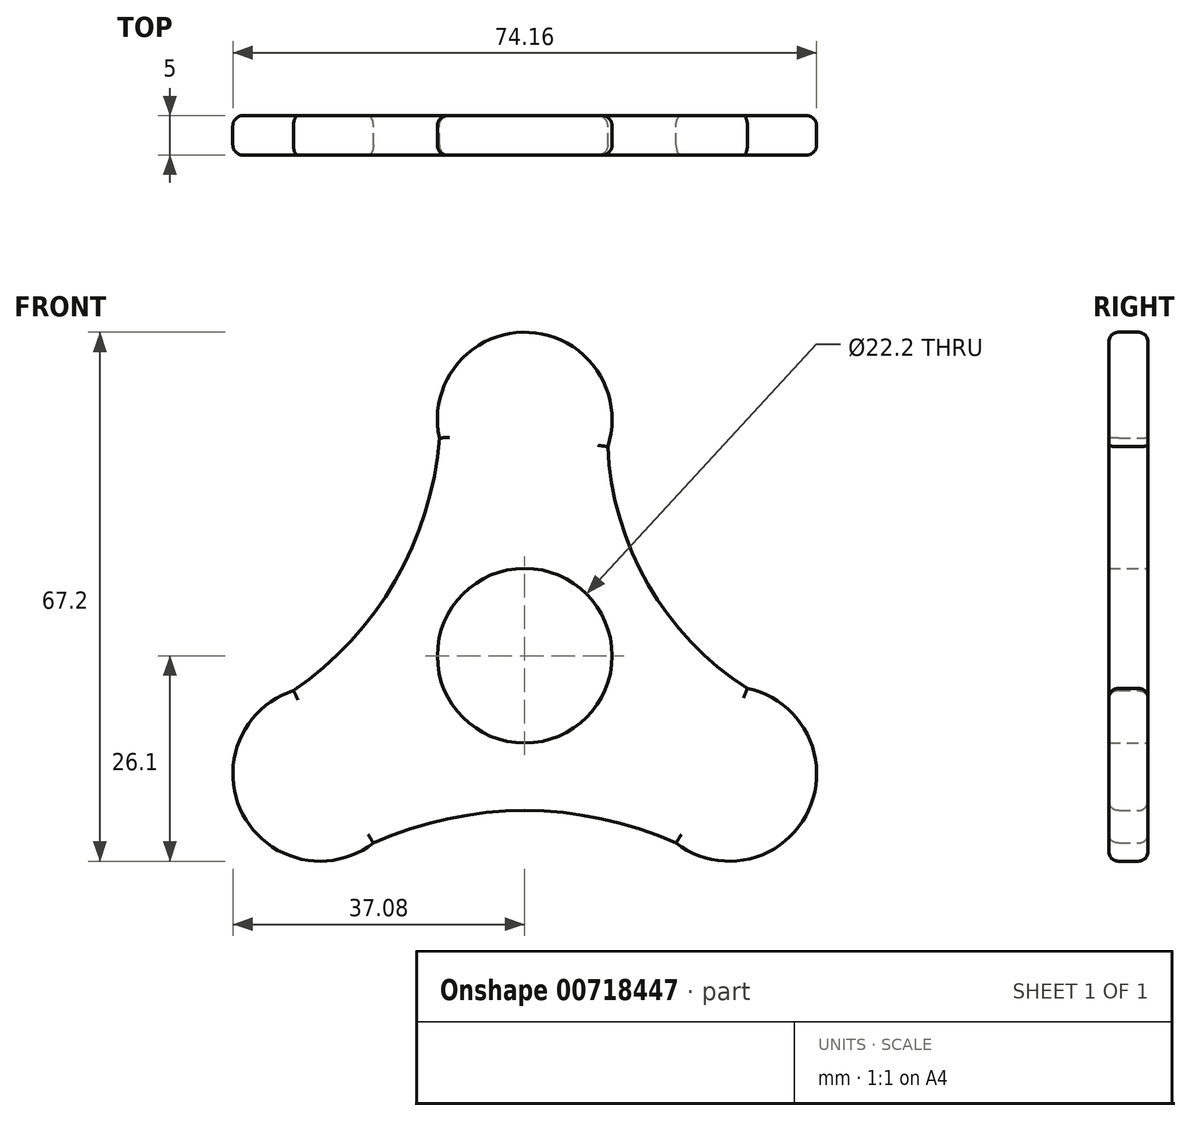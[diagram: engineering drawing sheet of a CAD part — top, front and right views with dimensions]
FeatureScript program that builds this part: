
annotation { "Feature Type Name" : "Feature", "Feature Type Description" : "" }
export const myFeature = defineFeature(function(context is Context, id is Id, definition is map)
    precondition{}
    {
        {
            var Q0;
            Q0=qCreatedBy(makeId("Front.planeOp"),FACE);
            var sketch = newSketch(context, id + "F0", { "sketchPlane" : qUnion([Q0])});
            skCircle(sketch, "E0", {"center": v(0, 0) * mm, "radius": 11.1 * mm});
            skArc(sketch, "E1", {"start": v(10.55, 26.56) * mm, "mid": v(0.57, 41.09) * mm, "end": v(-10.85, 27.66) * mm});
            skArc(sketch, "E2.1.0", {"start": v(-29.38, -4.43) * mm, "mid": v(-35.81, -20.15) * mm, "end": v(-19.22, -23.8) * mm});
            skArc(sketch, "E2.2.0", {"start": v(19.22, -23.8) * mm, "mid": v(36.06, -19.64) * mm, "end": v(28.28, -4.14) * mm});
            skArc(sketch, "E3", {"start": v(-33.69, -7.01) * mm, "mid": v(-16.45, 9.5) * mm, "end": v(-10.77, 32.68) * mm});
            skArc(sketch, "E4", {"start": v(10.77, 32.68) * mm, "mid": v(15.67, 9.04) * mm, "end": v(33.69, -7.01) * mm});
            skArc(sketch, "E5", {"start": v(22.91, -25.67) * mm, "mid": v(0, -19.68) * mm, "end": v(-22.91, -25.67) * mm});
            skSolve(sketch);
        }
        {
            var Q0;
            Q0 = qSketchRegion(id + "F0", true);
            extrude(context, id + "F1", {"entities" : qUnion([Q0]), "depth" : 5 * mm, "offsetDistance" : 25 * mm});
        }
        {
            var Q0;
            Q0=makeQuery(id+"F1.opExtrude","CAP_EDGE",EDGE,{"disambiguationData":[OSD([sQuery(id+"F0.wireOp",EDGE,"E4")])],"isStart":false});
            var Q1;
            Q1=makeQuery(id+"F1.opExtrude","CAP_EDGE",EDGE,{"disambiguationData":[OSD([sQuery(id+"F0.wireOp",EDGE,"E2.2.0")])],"isStart":false});
            var Q2;
            Q2=makeQuery(id+"F1.opExtrude","CAP_EDGE",EDGE,{"disambiguationData":[OSD([sQuery(id+"F0.wireOp",EDGE,"E3")])],"isStart":false});
            var Q3;
            Q3=makeQuery(id+"F1.opExtrude","CAP_EDGE",EDGE,{"disambiguationData":[OSD([sQuery(id+"F0.wireOp",EDGE,"E5")])],"isStart":false});
            var Q4;
            Q4=makeQuery(id+"F1.opExtrude","CAP_EDGE",EDGE,{"disambiguationData":[OSD([sQuery(id+"F0.wireOp",EDGE,"E3")])],"isStart":true});
            var Q5;
            Q5=makeQuery(id+"F1.opExtrude","CAP_EDGE",EDGE,{"disambiguationData":[OSD([sQuery(id+"F0.wireOp",EDGE,"E4")])],"isStart":true});
            var Q6;
            Q6=makeQuery(id+"F1.opExtrude","CAP_EDGE",EDGE,{"disambiguationData":[OSD([sQuery(id+"F0.wireOp",EDGE,"E5")])],"isStart":true});
            fillet(context, id + "F2", {"entities" : qUnion([Q0, Q1, Q2, Q3, Q4, Q5, Q6]), "radius" : 1.27 * mm, "tangentPropagation" : true, "allowEdgeOverflow" : false});
        }
        {
            var Q0;
            Q0=makeQuery(id+"F1.opExtrude","CAP_EDGE",EDGE,{"disambiguationData":[OSD([sQuery(id+"F0.wireOp",EDGE,"E1")])],"isStart":false});
            var Q1;
            Q1=makeQuery(id+"F1.opExtrude","CAP_EDGE",EDGE,{"disambiguationData":[OSD([sQuery(id+"F0.wireOp",EDGE,"E2.1.0")])],"isStart":false});
            var Q2;
            Q2=makeQuery(id+"F1.opExtrude","CAP_EDGE",EDGE,{"disambiguationData":[OSD([sQuery(id+"F0.wireOp",EDGE,"E2.2.0")])],"isStart":true});
            var Q3;
            Q3=makeQuery(id+"F1.opExtrude","CAP_EDGE",EDGE,{"disambiguationData":[OSD([sQuery(id+"F0.wireOp",EDGE,"E2.1.0")])],"isStart":true});
            var Q4;
            Q4=makeQuery(id+"F1.opExtrude","CAP_EDGE",EDGE,{"disambiguationData":[OSD([sQuery(id+"F0.wireOp",EDGE,"E1")])],"isStart":true});
            fillet(context, id + "F3", {"entities" : qUnion([Q0, Q1, Q2, Q3, Q4]), "radius" : 1.27 * mm, "tangentPropagation" : true, "allowEdgeOverflow" : false});
        }
    });
